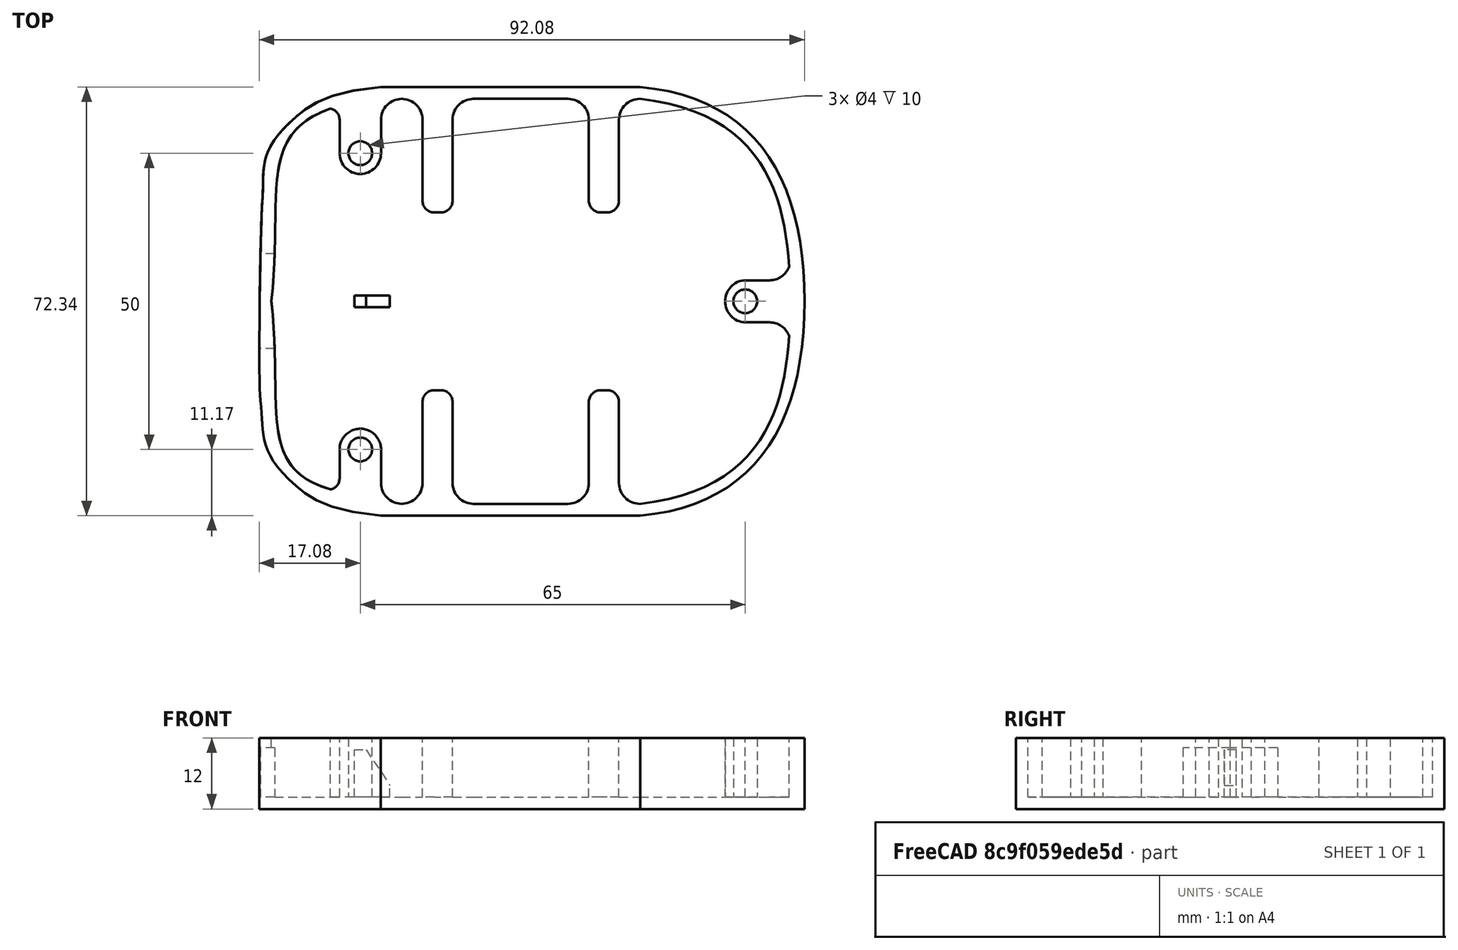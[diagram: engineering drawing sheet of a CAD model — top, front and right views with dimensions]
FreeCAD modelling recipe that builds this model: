
FCSTD DOCUMENT  (FreeCAD 1.0R39319 (Git))
Label: Makita LXT  - 18V - Bottom
License: Creative Commons Attribution 4.0
LicenseURL: https://creativecommons.org/licenses/by/4.0/
objects: Sketcher::SketchObject×6, PartDesign::Pad×4, PartDesign::Pocket×2, Mesh::Feature×1, Part::Feature×1, PartDesign::Body×1
note: 32 computed .brp shape members not serialized (recipe doc carries the construction recipe); baked Part::Feature solids carry a one-line shape summary decoded from their .brp

FEATURE [Mesh::Feature] XT60_top
  Placement = pos=(-27.475,0,0) rot=(0,0,1;0rad)
FEATURE [Sketcher::SketchObject] Sketch
  ArcFitTolerance = 0
  AttachmentSupport = -> [XY_Plane]
  FullyConstrained = false
  MakeInternals = false
  MapMode = 5
  sketch-geometry (88):
    g0: LineSegment StartX=20.4506 StartY=36.165 StartZ=0 EndX=64.2519 EndY=36.165 EndZ=0
    g1: GeomPoint [constr] X=92 Y=0 Z=0
    g2: GeomPoint [constr] X=64.2519 Y=36.165 Z=0
    g3: BSplineCurve PolesCount=4 KnotsCount=2 Degree=3 IsPeriodic=0
    g4-g7: Circle [constr] x4 (B-spline internal-alignment scaffolding for g3; pole/knot coordinates omitted)
    g8: GeomPoint [constr] X=20.4506 Y=36.165 Z=0
    g9: GeomPoint [constr] X=0 Y=0 Z=0
    g10: BSplineCurve PolesCount=6 KnotsCount=4 Degree=3 IsPeriodic=0
    g11: Circle [constr] CenterX=20.4506 CenterY=36.165 CenterZ=0 NormalX=0 NormalY=0 NormalZ=1 AngleXU=0 Radius=1
    g12: Circle [constr] CenterX=0 CenterY=0 CenterZ=0 NormalX=0 NormalY=0 NormalZ=1 AngleXU=0 Radius=1
    g13: Circle [constr] CenterX=11.7131 CenterY=35.4337 CenterZ=0 NormalX=0 NormalY=0 NormalZ=1 AngleXU=0 Radius=1
    g14: GeomPoint [constr] X=6.34276 Y=31.3033 Z=0
    g15: Circle [constr] CenterX=-0.951437 CenterY=26.4585 CenterZ=0 NormalX=0 NormalY=0 NormalZ=1 AngleXU=0 Radius=1
    g16: Circle [constr] CenterX=1.16814 CenterY=21.7363 CenterZ=0 NormalX=0 NormalY=0 NormalZ=1 AngleXU=0 Radius=1
    g17: Circle [constr] CenterX=0.212556 CenterY=14.5919 CenterZ=0 NormalX=0 NormalY=0 NormalZ=1 AngleXU=0 Radius=1
    g18: GeomPoint [constr] X=0.474517 Y=17.0951 Z=0
    g19: Circle CenterX=17 CenterY=25 CenterZ=0 NormalX=0 NormalY=0 NormalZ=1 AngleXU=0 Radius=2
    g20: ArcOfCircle CenterX=17 CenterY=25 CenterZ=0 NormalX=0 NormalY=0 NormalZ=1 AngleXU=0 Radius=3.5 StartAngle=3.14159 EndAngle=6.28319
    g21: LineSegment StartX=24 StartY=34.165 StartZ=0 EndX=64.1766 EndY=34.165 EndZ=0
    g22: BSplineCurve PolesCount=4 KnotsCount=2 Degree=3 IsPeriodic=0
    g23: BSplineCurve PolesCount=4 KnotsCount=2 Degree=3 IsPeriodic=0
    g24: LineSegment StartX=20.5 StartY=25 StartZ=0 EndX=20.5 EndY=30.665 EndZ=0
    g25: LineSegment StartX=13.5 StartY=25 StartZ=0 EndX=13.5 EndY=30.665 EndZ=0
    g26: ArcOfCircle CenterX=24 CenterY=30.665 CenterZ=0 NormalX=0 NormalY=0 NormalZ=1 AngleXU=0 Radius=3.5 StartAngle=1.5708 EndAngle=3.14159
    g27: ArcOfCircle CenterX=11.5973 CenterY=30.665 CenterZ=0 NormalX=0 NormalY=0 NormalZ=1 AngleXU=0 Radius=1.90272 StartAngle=3e-16 EndAngle=1.37116
    g28-g31: Circle [constr] x4 (B-spline internal-alignment scaffolding for g22; pole/knot coordinates omitted)
    g32: GeomPoint [constr] X=2 Y=0 Z=0
    g33: GeomPoint [constr] X=11.9746 Y=32.5299 Z=0
    g34: ArcOfCircle CenterX=82 CenterY=0 CenterZ=0 NormalX=0 NormalY=0 NormalZ=1 AngleXU=0 Radius=2 StartAngle=0 EndAngle=3.14159
    g35: ArcOfCircle CenterX=82.1093 CenterY=0.0523263 CenterZ=0 NormalX=0 NormalY=0 NormalZ=1 AngleXU=0 Radius=3.5 StartAngle=1.60202 EndAngle=3.15654
    g36: LineSegment StartX=82 StartY=3.55062 StartZ=0 EndX=86.1141 EndY=3.55062 EndZ=0
    g37: ArcOfCircle CenterX=86.1141 CenterY=7.05062 CenterZ=0 NormalX=0 NormalY=0 NormalZ=1 AngleXU=0 Radius=3.5 StartAngle=4.71239 EndAngle=5.92725
    g38-g41: Circle [constr] x4 (B-spline internal-alignment scaffolding for g23; pole/knot coordinates omitted)
    g42: GeomPoint [constr] X=64.1766 Y=34.165 Z=0
    g43: GeomPoint [constr] X=89.3947 Y=5.83098 Z=0
    g44: LineSegment StartX=20.4506 StartY=-36.165 StartZ=0 EndX=64.2519 EndY=-36.165 EndZ=0
    g45: GeomPoint [constr] X=92 Y=0 Z=0
    g46: GeomPoint [constr] X=64.2519 Y=-36.165 Z=0
    g47: BSplineCurve PolesCount=4 KnotsCount=2 Degree=3 IsPeriodic=0
    g48-g51: Circle [constr] x4 (B-spline internal-alignment scaffolding for g47; pole/knot coordinates omitted)
    g52: GeomPoint [constr] X=20.4506 Y=-36.165 Z=0
    g53: GeomPoint [constr] X=0 Y=0 Z=0
    g54: BSplineCurve PolesCount=6 KnotsCount=4 Degree=3 IsPeriodic=0
    g55: Circle [constr] CenterX=20.4506 CenterY=-36.165 CenterZ=0 NormalX=0 NormalY=0 NormalZ=1 AngleXU=0 Radius=1
    g56: Circle [constr] CenterX=0 CenterY=0 CenterZ=0 NormalX=0 NormalY=0 NormalZ=1 AngleXU=0 Radius=1
    g57: Circle [constr] CenterX=11.7131 CenterY=-35.4337 CenterZ=0 NormalX=0 NormalY=0 NormalZ=1 AngleXU=0 Radius=1
    g58: GeomPoint [constr] X=6.34276 Y=-31.3033 Z=0
    g59: Circle [constr] CenterX=-0.951437 CenterY=-26.4585 CenterZ=0 NormalX=0 NormalY=0 NormalZ=1 AngleXU=0 Radius=1
    g60: Circle [constr] CenterX=1.16814 CenterY=-21.7363 CenterZ=0 NormalX=0 NormalY=0 NormalZ=1 AngleXU=0 Radius=1
    g61: Circle [constr] CenterX=-0.212556 CenterY=-14.5919 CenterZ=0 NormalX=0 NormalY=0 NormalZ=1 AngleXU=0 Radius=1
    g62: GeomPoint [constr] X=0.190914 Y=-17.0951 Z=0
    g63: Circle CenterX=17 CenterY=-25 CenterZ=0 NormalX=0 NormalY=0 NormalZ=1 AngleXU=0 Radius=2
    g64: ArcOfCircle CenterX=17 CenterY=-25 CenterZ=0 NormalX=0 NormalY=0 NormalZ=1 AngleXU=0 Radius=3.5 StartAngle=6.28318 EndAngle=9.43706
    g65: LineSegment StartX=24 StartY=-34.165 StartZ=0 EndX=64.1766 EndY=-34.165 EndZ=0
    g66: BSplineCurve PolesCount=4 KnotsCount=2 Degree=3 IsPeriodic=0
    g67: BSplineCurve PolesCount=4 KnotsCount=2 Degree=3 IsPeriodic=0
    g68: LineSegment StartX=20.5 StartY=-25 StartZ=0 EndX=20.5 EndY=-30.665 EndZ=0
    g69: LineSegment StartX=13.5003 StartY=-25.043 StartZ=0 EndX=13.5003 EndY=-29.8713 EndZ=0
    g70: ArcOfCircle CenterX=24 CenterY=-30.665 CenterZ=0 NormalX=0 NormalY=0 NormalZ=1 AngleXU=0 Radius=3.5 StartAngle=3.14159 EndAngle=4.71239
    g71: ArcOfCircle CenterX=11.5854 CenterY=-29.8713 CenterZ=0 NormalX=0 NormalY=0 NormalZ=1 AngleXU=0 Radius=1.91491 StartAngle=4.91041 EndAngle=6.28319
    g72-g75: Circle [constr] x4 (B-spline internal-alignment scaffolding for g66; pole/knot coordinates omitted)
    g76: GeomPoint [constr] X=2 Y=0 Z=0
    g77: GeomPoint [constr] X=11.9621 Y=-31.7488 Z=0
    g78: ArcOfCircle CenterX=82 CenterY=-6.33246e-08 CenterZ=0 NormalX=0 NormalY=0 NormalZ=1 AngleXU=0 Radius=2 StartAngle=3.14159 EndAngle=6.28319
    g79: ArcOfCircle CenterX=82.1092 CenterY=-0.0531578 CenterZ=0 NormalX=0 NormalY=0 NormalZ=1 AngleXU=0 Radius=3.5 StartAngle=3.1264 EndAngle=4.68277
    g80: LineSegment StartX=82.0056 StartY=-3.55162 StartZ=0 EndX=86.1145 EndY=-3.55162 EndZ=0
    g81: ArcOfCircle CenterX=86.1145 CenterY=-7.05162 CenterZ=0 NormalX=0 NormalY=0 NormalZ=1 AngleXU=0 Radius=3.5 StartAngle=0.356241 EndAngle=1.5708
    g82-g85: Circle [constr] x4 (B-spline internal-alignment scaffolding for g67; pole/knot coordinates omitted)
    g86: GeomPoint [constr] X=64.1766 Y=-34.165 Z=0
    g87: GeomPoint [constr] X=89.3947 Y=-5.83098 Z=0
  constraints (167):
    c: Horizontal(g0)
    c: PointOnObject(g3,g-1)
    c: Coincident(g3,g0)
    c: InternalAlignment(g1,g3)
    c: InternalAlignment(g2,g3)
    c: InternalAlignment(g4,g3)
    c: Weight(g4) = 1
    c: InternalAlignment(g5,g3)
    c: Equal(g5,g4)
    c: InternalAlignment(g6,g3)
    c: Equal(g6,g4)
    c: InternalAlignment(g7,g3)
    c: Equal(g7,g4)
    c: Coincident(g10,g0)
    c: Coincident(g10,g-1)
    c: InternalAlignment(g8,g10)
    c: InternalAlignment(g9,g10)
    c: InternalAlignment(g11,g10)
    c: Weight(g11) = 1
    c: InternalAlignment(g12,g10)
    c: Equal(g12,g11)
    c: InternalAlignment(g13,g10)
    c: Equal(g13,g11)
    c: InternalAlignment(g14,g10)
    c: InternalAlignment(g15,g10)
    c: Equal(g15,g11)
    c: InternalAlignment(g16,g10)
    c: Equal(g16,g11)
    c: InternalAlignment(g17,g10)
    c: Equal(g17,g11)
    c: InternalAlignment(g18,g10)
    c: Coincident(g20,g19)
    c: Horizontal(g20,g19)
    c: Horizontal(g19,g20)
    c: Horizontal(g21)
    c: PointOnObject(g22,g-1)
    c: Coincident(g23,g21)
    c: DistanceY(g21,g0) = 2
    c: DistanceX(g10,g22) = 2
    c: Coincident(g24,g20)
    c: Vertical(g24)
    c: Coincident(g25,g20)
    c: Vertical(g25)
    c: Tangent(g26,g24) = 1.5708
    c: Tangent(g27,g25) = -1.5708
    c: Horizontal(g24,g25)
    c: Equal(g20,g26)
    c: Coincident(g22,g27)
    c: InternalAlignment(g28,g22)
    c: Weight(g28) = 1
    c: InternalAlignment(g29,g22)
    c: Equal(g29,g28)
    c: InternalAlignment(g30,g22)
    c: Equal(g30,g28)
    c: InternalAlignment(g31,g22)
    c: Equal(g31,g28)
    c: InternalAlignment(g32,g22)
    c: InternalAlignment(g33,g22)
    c: Tangent(g21,g26) = 1.5708
    c: PointOnObject(g34,g-1)
    c: PointOnObject(g34,g-1)
    c: PointOnObject(g34,g-1)
    c: Equal(g19,g34)
    c: Diameter(g19) = 4
    c: Diameter(g20) = 7
    c: PointOnObject(g35,g-1)
    c: Vertical(g34,g35)
    c: Equal(g35,g20)
    c: Coincident(g36,g35)
    c: Horizontal(g36)
    c: Tangent(g37,g36) = -1.5708
    c: Equal(g35,g37)
    c: Coincident(g23,g37)
    c: InternalAlignment(g38,g23)
    c: Weight(g38) = 1
    c: InternalAlignment(g39,g23)
    c: Equal(g39,g38)
    c: InternalAlignment(g40,g23)
    c: Equal(g40,g38)
    c: InternalAlignment(g41,g23)
    c: Equal(g41,g38)
    c: InternalAlignment(g42,g23)
    c: InternalAlignment(g43,g23)
    c: Horizontal(g44)
    c: Coincident(g47,g44)
    c: InternalAlignment(g45,g47)
    c: InternalAlignment(g46,g47)
    c: InternalAlignment(g48,g47)
    c: Weight(g48) = 1
    c: InternalAlignment(g49,g47)
    c: Equal(g49,g48)
    c: InternalAlignment(g50,g47)
    c: Equal(g50,g48)
    c: InternalAlignment(g51,g47)
    c: Equal(g51,g48)
    c: Coincident(g54,g44)
    c: InternalAlignment(g52,g54)
    c: InternalAlignment(g53,g54)
    c: InternalAlignment(g55,g54)
    c: Weight(g55) = 1
    c: InternalAlignment(g56,g54)
    c: Equal(g56,g55)
    c: InternalAlignment(g57,g54)
    c: Equal(g57,g55)
    c: InternalAlignment(g58,g54)
    c: InternalAlignment(g59,g54)
    c: Equal(g59,g55)
    c: InternalAlignment(g60,g54)
    c: Equal(g60,g55)
    c: InternalAlignment(g61,g54)
    c: Equal(g61,g55)
    c: InternalAlignment(g62,g54)
    c: Coincident(g64,g63)
    c: Horizontal(g65)
    c: Coincident(g67,g65)
    c: Coincident(g68,g64)
    c: Vertical(g68)
    c: Coincident(g69,g64)
    c: Vertical(g69)
    c: Tangent(g70,g68) = -1.5708
    c: Tangent(g71,g69) = 1.5708
    c: Equal(g64,g70)
    c: Coincident(g66,g71)
    c: InternalAlignment(g72,g66)
    c: Weight(g72) = 1
    c: InternalAlignment(g73,g66)
    c: Equal(g73,g72)
    c: InternalAlignment(g74,g66)
    c: Equal(g74,g72)
    c: InternalAlignment(g75,g66)
    c: Equal(g75,g72)
    c: InternalAlignment(g76,g66)
    c: InternalAlignment(g77,g66)
    c: Tangent(g65,g70) = -1.5708
    c: Equal(g63,g78)
    c: Diameter(g63) = 4
    c: Diameter(g64) = 7
    c: Equal(g79,g64)
    c: Coincident(g80,g79)
    c: Horizontal(g80)
    c: Tangent(g81,g80) = 1.5708
    c: Equal(g79,g81)
    c: Coincident(g67,g81)
    c: InternalAlignment(g82,g67)
    c: Weight(g82) = 1
    c: InternalAlignment(g83,g67)
    c: Equal(g83,g82)
    c: InternalAlignment(g84,g67)
    c: Equal(g84,g82)
    c: InternalAlignment(g85,g67)
    c: Equal(g85,g82)
    c: InternalAlignment(g86,g67)
    c: InternalAlignment(g87,g67)
    c: DistanceY(g44,g0) = 72.33
    c: DistanceY(g63,g19) = 50
    c: DistanceX(g19) = 17
    c: Symmetric(g63,g19,g-1)
    c: DistanceX(g19,g34) = 65
    c: DistanceX(g54,g3) = 92
    c: Coincident(g79,g35)
    c: Coincident(g34,g78)
    c: Coincident(g78,g34)
    c: Tangent(g54,g10) = 1.5708
    c: Tangent(g47,g3) = 1.5708
    c: Symmetric(g0,g44,g-1)
    c: Symmetric(g65,g21,g-1)
    c: Symmetric(g23,g67,g-1)
FEATURE [Part::Feature] XT60_top001
  shape: bbox 92.05 x 71 x 12 mm, 4368 faces, 0 solids (baked)
FEATURE [PartDesign::Pad] Pad
  Direction = (0,0,1)
  Length = 10
  Length2 = 10
  Profile = -> Sketch
  ReferenceAxis = -> Sketch [N_Axis]
  Suppressed = false
  Type = 0
FEATURE [Sketcher::SketchObject] Sketch004
  ArcFitTolerance = 0
  AttachmentSupport = -> [XY_Plane]
  FullyConstrained = false
  MakeInternals = false
  MapMode = 5
  sketch-geometry (38):
    g0: LineSegment StartX=20.4506 StartY=36.165 StartZ=0 EndX=64.2519 EndY=36.165 EndZ=0
    g1: GeomPoint [constr] X=92 Y=0 Z=0
    g2: GeomPoint [constr] X=64.2519 Y=36.165 Z=0
    g3: BSplineCurve PolesCount=4 KnotsCount=2 Degree=3 IsPeriodic=0
    g4-g7: Circle [constr] x4 (B-spline internal-alignment scaffolding for g3; pole/knot coordinates omitted)
    g8: GeomPoint [constr] X=20.4506 Y=36.165 Z=0
    g9: GeomPoint [constr] X=0 Y=0 Z=0
    g10: BSplineCurve PolesCount=6 KnotsCount=4 Degree=3 IsPeriodic=0
    g11: Circle [constr] CenterX=20.4506 CenterY=36.165 CenterZ=0 NormalX=0 NormalY=0 NormalZ=1 AngleXU=0 Radius=1
    g12: Circle [constr] CenterX=0 CenterY=0 CenterZ=0 NormalX=0 NormalY=0 NormalZ=1 AngleXU=0 Radius=1
    g13: Circle [constr] CenterX=11.7131 CenterY=35.4337 CenterZ=0 NormalX=0 NormalY=0 NormalZ=1 AngleXU=0 Radius=1
    g14: GeomPoint [constr] X=6.34276 Y=31.3033 Z=0
    g15: Circle [constr] CenterX=-0.951437 CenterY=26.4585 CenterZ=0 NormalX=0 NormalY=0 NormalZ=1 AngleXU=0 Radius=1
    g16: Circle [constr] CenterX=1.16814 CenterY=21.7363 CenterZ=0 NormalX=0 NormalY=0 NormalZ=1 AngleXU=0 Radius=1
    g17: Circle [constr] CenterX=0.212556 CenterY=14.5919 CenterZ=0 NormalX=0 NormalY=0 NormalZ=1 AngleXU=0 Radius=1
    g18: GeomPoint [constr] X=0.474517 Y=17.0951 Z=0
    g19: LineSegment StartX=20.4506 StartY=-36.165 StartZ=0 EndX=64.2519 EndY=-36.165 EndZ=0
    g20: GeomPoint [constr] X=92 Y=0 Z=0
    g21: GeomPoint [constr] X=64.2519 Y=-36.165 Z=0
    g22: BSplineCurve PolesCount=4 KnotsCount=2 Degree=3 IsPeriodic=0
    g23-g26: Circle [constr] x4 (B-spline internal-alignment scaffolding for g22; pole/knot coordinates omitted)
    g27: GeomPoint [constr] X=20.4506 Y=-36.165 Z=0
    g28: GeomPoint [constr] X=0 Y=0 Z=0
    g29: BSplineCurve PolesCount=6 KnotsCount=4 Degree=3 IsPeriodic=0
    g30: Circle [constr] CenterX=20.4506 CenterY=-36.165 CenterZ=0 NormalX=0 NormalY=0 NormalZ=1 AngleXU=0 Radius=1
    g31: Circle [constr] CenterX=0 CenterY=0 CenterZ=0 NormalX=0 NormalY=0 NormalZ=1 AngleXU=0 Radius=1
    g32: Circle [constr] CenterX=11.7131 CenterY=-35.4337 CenterZ=0 NormalX=0 NormalY=0 NormalZ=1 AngleXU=0 Radius=1
    g33: GeomPoint [constr] X=6.34276 Y=-31.3033 Z=0
    g34: Circle [constr] CenterX=-0.951437 CenterY=-26.4585 CenterZ=0 NormalX=0 NormalY=0 NormalZ=1 AngleXU=0 Radius=1
    g35: Circle [constr] CenterX=1.16814 CenterY=-21.7363 CenterZ=0 NormalX=0 NormalY=0 NormalZ=1 AngleXU=0 Radius=1
    g36: Circle [constr] CenterX=-0.212556 CenterY=-14.5919 CenterZ=0 NormalX=0 NormalY=0 NormalZ=1 AngleXU=0 Radius=1
    g37: GeomPoint [constr] X=0.190914 Y=-17.0951 Z=0
  constraints (65):
    c: Horizontal(g0)
    c: PointOnObject(g3,g-1)
    c: Coincident(g3,g0)
    c: InternalAlignment(g1,g3)
    c: InternalAlignment(g2,g3)
    c: InternalAlignment(g4,g3)
    c: Weight(g4) = 1
    c: InternalAlignment(g5,g3)
    c: Equal(g5,g4)
    c: InternalAlignment(g6,g3)
    c: Equal(g6,g4)
    c: InternalAlignment(g7,g3)
    c: Equal(g7,g4)
    c: Coincident(g10,g0)
    c: Coincident(g10,g-1)
    c: InternalAlignment(g8,g10)
    c: InternalAlignment(g9,g10)
    c: InternalAlignment(g11,g10)
    c: Weight(g11) = 1
    c: InternalAlignment(g12,g10)
    c: Equal(g12,g11)
    c: InternalAlignment(g13,g10)
    c: Equal(g13,g11)
    c: InternalAlignment(g14,g10)
    c: InternalAlignment(g15,g10)
    c: Equal(g15,g11)
    c: InternalAlignment(g16,g10)
    c: Equal(g16,g11)
    c: InternalAlignment(g17,g10)
    c: Equal(g17,g11)
    c: InternalAlignment(g18,g10)
    c: Horizontal(g19)
    c: Coincident(g22,g19)
    c: InternalAlignment(g20,g22)
    c: InternalAlignment(g21,g22)
    c: InternalAlignment(g23,g22)
    c: Weight(g23) = 1
    c: InternalAlignment(g24,g22)
    c: Equal(g24,g23)
    c: InternalAlignment(g25,g22)
    c: Equal(g25,g23)
    c: InternalAlignment(g26,g22)
    c: Equal(g26,g23)
    c: Coincident(g29,g19)
    c: InternalAlignment(g27,g29)
    c: InternalAlignment(g28,g29)
    c: InternalAlignment(g30,g29)
    c: Weight(g30) = 1
    c: InternalAlignment(g31,g29)
    c: Equal(g31,g30)
    c: InternalAlignment(g32,g29)
    c: Equal(g32,g30)
    c: InternalAlignment(g33,g29)
    c: InternalAlignment(g34,g29)
    c: Equal(g34,g30)
    c: InternalAlignment(g35,g29)
    c: Equal(g35,g30)
    c: InternalAlignment(g36,g29)
    c: Equal(g36,g30)
    c: InternalAlignment(g37,g29)
    c: DistanceY(g19,g0) = 72.33
    c: DistanceX(g29,g3) = 92
    c: Tangent(g29,g10) = 1.5708
    c: Tangent(g22,g3) = 1.5708
    c: Symmetric(g0,g19,g-1)
FEATURE [PartDesign::Pad] Pad001
  BaseFeature = -> Pad
  Direction = (0,0,1)
  Length = 2
  Length2 = 10
  Profile = -> Sketch004
  ReferenceAxis = -> Sketch004 [N_Axis]
  Refine = true
  Reversed = true
  Suppressed = false
  Type = 0
FEATURE [Sketcher::SketchObject] Sketch003
  ArcFitTolerance = 1e-06
  ExternalGeometry = -> [Pad001]
  FullyConstrained = false
  MakeInternals = false
  MapMode = 5
  sketch-geometry (32):
    g0: LineSegment StartX=24 StartY=34.165 StartZ=0 EndX=36.0883 EndY=34.165 EndZ=0
    g1: LineSegment StartX=52.0883 StartY=34.165 StartZ=0 EndX=64.1766 EndY=34.165 EndZ=0
    g2: LineSegment StartX=60.6766 StartY=30.665 StartZ=0 EndX=60.6766 EndY=17 EndZ=0
    g3: LineSegment StartX=58.6766 StartY=15 StartZ=0 EndX=57.5883 EndY=15 EndZ=0
    g4: LineSegment StartX=55.5883 StartY=17 StartZ=0 EndX=55.5883 EndY=30.665 EndZ=0
    g5: LineSegment StartX=32.5883 StartY=30.665 StartZ=0 EndX=32.5883 EndY=17 EndZ=0
    g6: LineSegment StartX=27.5 StartY=30.665 StartZ=0 EndX=27.5 EndY=17 EndZ=0
    g7: LineSegment StartX=29.5 StartY=15 StartZ=0 EndX=30.5883 EndY=15 EndZ=0
    g8: ArcOfCircle CenterX=24 CenterY=30.665 CenterZ=0 NormalX=0 NormalY=0 NormalZ=1 AngleXU=0 Radius=3.5 StartAngle=3e-16 EndAngle=1.5708
    g9: ArcOfCircle CenterX=36.0883 CenterY=30.665 CenterZ=0 NormalX=0 NormalY=0 NormalZ=1 AngleXU=0 Radius=3.5 StartAngle=1.5708 EndAngle=3.14159
    g10: ArcOfCircle CenterX=52.0883 CenterY=30.665 CenterZ=0 NormalX=0 NormalY=0 NormalZ=1 AngleXU=0 Radius=3.5 StartAngle=4e-16 EndAngle=1.5708
    g11: ArcOfCircle CenterX=64.1766 CenterY=30.665 CenterZ=0 NormalX=0 NormalY=0 NormalZ=1 AngleXU=0 Radius=3.5 StartAngle=1.5708 EndAngle=3.14159
    g12: ArcOfCircle CenterX=58.6766 CenterY=17 CenterZ=0 NormalX=0 NormalY=0 NormalZ=1 AngleXU=0 Radius=2 StartAngle=4.71239 EndAngle=6.28319
    g13: ArcOfCircle CenterX=57.5883 CenterY=17 CenterZ=0 NormalX=0 NormalY=0 NormalZ=1 AngleXU=0 Radius=2 StartAngle=3.14159 EndAngle=4.71239
    g14: ArcOfCircle CenterX=30.5883 CenterY=17 CenterZ=0 NormalX=0 NormalY=0 NormalZ=1 AngleXU=0 Radius=2 StartAngle=4.71239 EndAngle=6.28319
    g15: ArcOfCircle CenterX=29.5 CenterY=17 CenterZ=0 NormalX=0 NormalY=0 NormalZ=1 AngleXU=0 Radius=2 StartAngle=3.14159 EndAngle=4.71239
    g16: LineSegment StartX=24 StartY=-34.165 StartZ=0 EndX=36.0883 EndY=-34.165 EndZ=0
    g17: LineSegment StartX=52.0883 StartY=-34.165 StartZ=0 EndX=64.1766 EndY=-34.165 EndZ=0
    g18: LineSegment StartX=60.6766 StartY=-30.665 StartZ=0 EndX=60.6766 EndY=-17 EndZ=0
    g19: LineSegment StartX=58.6766 StartY=-15 StartZ=0 EndX=57.5883 EndY=-15 EndZ=0
    g20: LineSegment StartX=55.5883 StartY=-17 StartZ=0 EndX=55.5883 EndY=-30.665 EndZ=0
    g21: LineSegment StartX=32.5883 StartY=-30.665 StartZ=0 EndX=32.5883 EndY=-17 EndZ=0
    g22: LineSegment StartX=27.5 StartY=-30.665 StartZ=0 EndX=27.5 EndY=-17 EndZ=0
    g23: LineSegment StartX=29.5 StartY=-15 StartZ=0 EndX=30.5883 EndY=-15 EndZ=0
    g24: ArcOfCircle CenterX=24 CenterY=-30.665 CenterZ=0 NormalX=0 NormalY=0 NormalZ=1 AngleXU=0 Radius=3.5 StartAngle=4.71239 EndAngle=6.28319
    g25: ArcOfCircle CenterX=36.0883 CenterY=-30.665 CenterZ=0 NormalX=0 NormalY=0 NormalZ=1 AngleXU=0 Radius=3.5 StartAngle=3.14159 EndAngle=4.71239
    g26: ArcOfCircle CenterX=52.0883 CenterY=-30.665 CenterZ=0 NormalX=0 NormalY=0 NormalZ=1 AngleXU=0 Radius=3.5 StartAngle=4.71239 EndAngle=6.28319
    g27: ArcOfCircle CenterX=64.1766 CenterY=-30.665 CenterZ=0 NormalX=0 NormalY=0 NormalZ=1 AngleXU=0 Radius=3.5 StartAngle=3.14159 EndAngle=4.71239
    g28: ArcOfCircle CenterX=58.6766 CenterY=-17 CenterZ=0 NormalX=0 NormalY=0 NormalZ=1 AngleXU=0 Radius=2 StartAngle=0 EndAngle=1.5708
    g29: ArcOfCircle CenterX=57.5883 CenterY=-17 CenterZ=0 NormalX=0 NormalY=0 NormalZ=1 AngleXU=0 Radius=2 StartAngle=1.5708 EndAngle=3.14159
    g30: ArcOfCircle CenterX=30.5883 CenterY=-17 CenterZ=0 NormalX=0 NormalY=0 NormalZ=1 AngleXU=0 Radius=2 StartAngle=0 EndAngle=1.5708
    g31: ArcOfCircle CenterX=29.5 CenterY=-17 CenterZ=0 NormalX=0 NormalY=0 NormalZ=1 AngleXU=0 Radius=2 StartAngle=1.5708 EndAngle=3.14159
  constraints (69):
    c: PointOnObject(g0,g-3)
    c: PointOnObject(g1,g-3)
    c: Vertical(g2)
    c: Horizontal(g3)
    c: Vertical(g4)
    c: Vertical(g5)
    c: Horizontal(g7)
    c: Equal(g1,g0)
    c: Coincident(g1,g-3)
    c: Coincident(g0,g-3)
    c: Vertical(g6)
    c: Equal(g6,g5)
    c: Equal(g5,g4)
    c: Equal(g4,g2)
    c: Tangent(g11,g1) = 1.5708
    c: Tangent(g10,g1) = 1.5708
    c: Tangent(g9,g0) = 1.5708
    c: Tangent(g8,g0) = 1.5708
    c: Tangent(g8,g6) = 1.5708
    c: Tangent(g9,g5) = -1.5708
    c: Tangent(g10,g4) = -1.5708
    c: Tangent(g11,g2) = -1.5708
    c: Equal(g8,g9)
    c: Equal(g9,g10)
    c: Equal(g10,g11)
    c: Tangent(g15,g6) = -1.5708
    c: Tangent(g15,g7) = -1.5708
    c: Tangent(g14,g7) = -1.5708
    c: Tangent(g14,g5) = 1.5708
    c: Tangent(g13,g4) = 1.5708
    c: Tangent(g13,g3) = 1.5708
    c: Tangent(g12,g3) = 1.5708
    c: Tangent(g12,g2) = 1.5708
    c: Equal(g-4,g8)
    c: DistanceY(g7) = 15
    c: Equal(g15,g13)
    c: Radius(g12) = 2
    c: DistanceX(g0,g1) = 16
    c: Vertical(g18)
    c: Horizontal(g19)
    c: Vertical(g20)
    c: Vertical(g21)
    c: Horizontal(g23)
    c: Equal(g17,g16)
    c: Vertical(g22)
    c: Equal(g22,g21)
    c: Equal(g21,g20)
    c: Equal(g20,g18)
    c: Tangent(g27,g17) = -1.5708
    c: Tangent(g26,g17) = -1.5708
    c: Tangent(g25,g16) = -1.5708
    c: Tangent(g24,g16) = -1.5708
    c: Tangent(g24,g22) = -1.5708
    c: Tangent(g25,g21) = 1.5708
    c: Tangent(g26,g20) = 1.5708
    c: Tangent(g27,g18) = 1.5708
    c: Equal(g24,g25)
    c: Equal(g25,g26)
    c: Equal(g26,g27)
    c: Tangent(g31,g22) = 1.5708
    c: Tangent(g31,g23) = 1.5708
    c: Tangent(g30,g23) = 1.5708
    c: Tangent(g30,g21) = -1.5708
    c: Tangent(g29,g20) = -1.5708
    c: Tangent(g29,g19) = -1.5708
    c: Tangent(g28,g19) = -1.5708
    c: Tangent(g28,g18) = -1.5708
    c: Equal(g31,g29)
    c: Radius(g28) = 2
FEATURE [PartDesign::Pad] Pad002
  BaseFeature = -> Pad001
  Direction = (0,0,1)
  Length = 10
  Length2 = 10
  Profile = -> Sketch003
  ReferenceAxis = -> Sketch003 [N_Axis]
  Refine = true
  Suppressed = false
  Type = 3
  UpToFace = -> Pad001 [Face4]
FEATURE [Sketcher::SketchObject] Sketch005
  ArcFitTolerance = 1e-06
  AttachmentSupport = -> [YZ_Plane]
  FullyConstrained = true
  MakeInternals = false
  MapMode = 5
  Placement = pos=(0,0,0) rot=(0.57735,0.57735,0.57735;2.0944rad)
  sketch-geometry (5):
    g0: LineSegment StartX=8 StartY=8.3 StartZ=0 EndX=-8 EndY=8.3 EndZ=0
    g1: LineSegment StartX=-8 StartY=8.3 StartZ=0 EndX=-8 EndY=0 EndZ=0
    g2: LineSegment StartX=-8 StartY=0 StartZ=0 EndX=8 EndY=0 EndZ=0
    g3: LineSegment StartX=8 StartY=0 StartZ=0 EndX=8 EndY=8.3 EndZ=0
    g4: GeomPoint [constr] X=1e-16 Y=4.15 Z=0
  constraints (13):
    c: Coincident(g0,g1)
    c: Coincident(g1,g2)
    c: Coincident(g2,g3)
    c: Coincident(g3,g0)
    c: Horizontal(g0)
    c: Horizontal(g2)
    c: Vertical(g1)
    c: Vertical(g3)
    c: Symmetric(g2,g0,g4)
    c: PointOnObject(g4,g-2)
    c: DistanceX(g0,g0) = 16
    c: DistanceY(g1,g1) = 8.3
    c: PointOnObject(g1,g-1)
FEATURE [PartDesign::Pocket] Pocket
  BaseFeature = -> Pad002
  Direction = (-1,0,0)
  Length = 8
  Length2 = 5
  Midplane = true
  Profile = -> Sketch005
  ReferenceAxis = -> Sketch005 [N_Axis]
  Refine = true
  Suppressed = false
  Type = 0
FEATURE [Sketcher::SketchObject] Sketch006
  ArcFitTolerance = 1e-06
  AttachmentSupport = -> [Pocket]
  FullyConstrained = true
  MakeInternals = false
  MapMode = 5
  sketch-geometry (5):
    g0: LineSegment StartX=16 StartY=1 StartZ=0 EndX=16 EndY=-1 EndZ=0
    g1: LineSegment StartX=16 StartY=-1 StartZ=0 EndX=22 EndY=-1 EndZ=0
    g2: LineSegment StartX=22 StartY=-1 StartZ=0 EndX=22 EndY=1 EndZ=0
    g3: LineSegment StartX=22 StartY=1 StartZ=0 EndX=16 EndY=1 EndZ=0
    g4: GeomPoint [constr] X=19 Y=0 Z=0
  constraints (13):
    c: Coincident(g0,g1)
    c: Coincident(g1,g2)
    c: Coincident(g2,g3)
    c: Coincident(g3,g0)
    c: Vertical(g0)
    c: Vertical(g2)
    c: Horizontal(g1)
    c: Horizontal(g3)
    c: Symmetric(g2,g0,g4)
    c: PointOnObject(g4,g-1)
    c: DistanceY(g2,g2) = 2
    c: DistanceX(g1,g1) = 6
    c: DistanceX(g0) = 16
FEATURE [PartDesign::Pad] Pad003
  BaseFeature = -> Pocket
  Direction = (0,0,1)
  Length = 8
  Length2 = 10
  Profile = -> Sketch006
  ReferenceAxis = -> Sketch006 [N_Axis]
  Refine = true
  Suppressed = false
  Type = 0
FEATURE [Sketcher::SketchObject] Sketch007
  ArcFitTolerance = 1e-06
  AttachmentSupport = -> [Pad003]
  ExternalGeometry = -> [Pad003]
  FullyConstrained = true
  MakeInternals = false
  MapMode = 5
  Placement = pos=(0,-1,0) rot=(1,0,0;1.5708rad)
  sketch-geometry (3):
    g0: LineSegment StartX=22 StartY=2 StartZ=0 EndX=22 EndY=8 EndZ=0
    g1: LineSegment StartX=22 StartY=8 StartZ=0 EndX=18 EndY=8 EndZ=0
    g2: LineSegment StartX=18 StartY=8 StartZ=0 EndX=22 EndY=2 EndZ=0
  constraints (8):
    c: Coincident(g0,g-3)
    c: Vertical(g0)
    c: Coincident(g0,g1)
    c: PointOnObject(g1,g-3)
    c: Coincident(g1,g2)
    c: Coincident(g2,g0)
    c: DistanceY(g0) = 2
    c: DistanceX(g-3,g1) = 2
FEATURE [PartDesign::Pocket] Pocket001
  BaseFeature = -> Pad003
  Direction = (0,1,-2e-16)
  Length = 5
  Length2 = 5
  Profile = -> Sketch007
  ReferenceAxis = -> Sketch007 [N_Axis]
  Refine = true
  Suppressed = false
  Type = 2
FEATURE [PartDesign::Body] Body  label="Single"
  AllowCompound = false
  Group = -> [Sketch,Pad,Sketch003,Sketch004,Pad001,Pad002,Sketch005,Pocket,Sketch006,Pad003,Sketch007,Pocket001]
  Origin = -> Origin
  Tip = -> Pocket001
